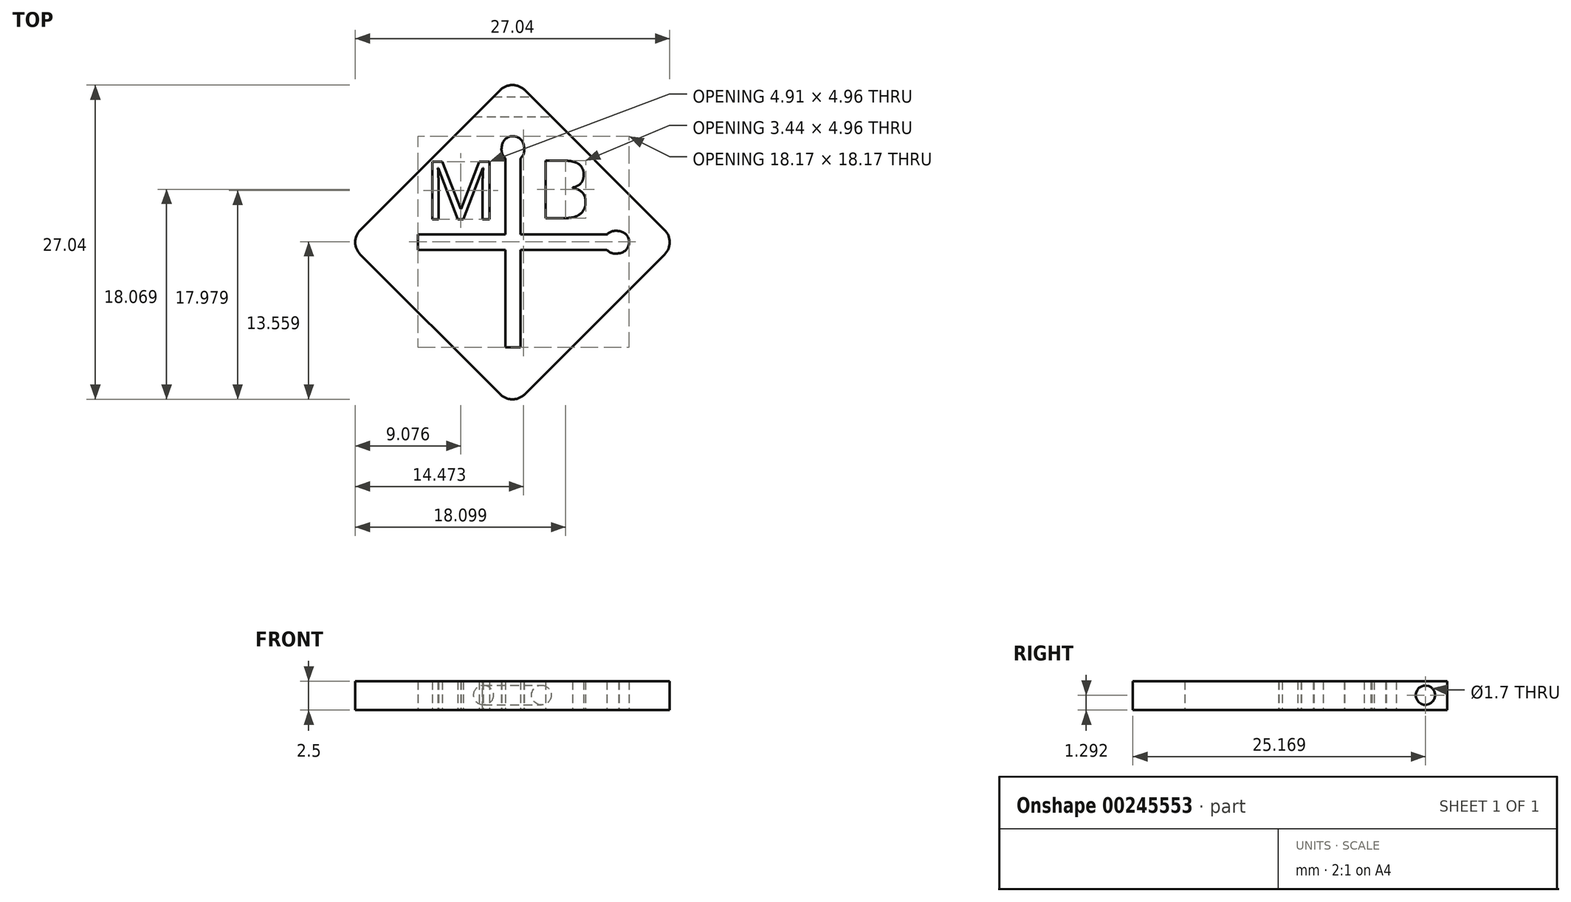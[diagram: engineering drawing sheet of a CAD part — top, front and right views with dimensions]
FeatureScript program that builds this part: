
annotation { "Feature Type Name" : "Feature", "Feature Type Description" : "" }
export const myFeature = defineFeature(function(context is Context, id is Id, definition is map)
    precondition{}
    {
        {
            var Q0;
            Q0=qCreatedBy(makeId("Top.planeOp"),FACE);
            var sketch = newSketch(context, id + "F0", { "sketchPlane" : qUnion([Q0])});
            skLineSegment(sketch, "E0", {"start": v(1.06, -1.06) * mm, "end": v(13.08, -13.08) * mm});
            skLineSegment(sketch, "E1", {"start": v(13.08, -15.2) * mm, "end": v(1.06, -27.22) * mm});
            skLineSegment(sketch, "E2", {"start": v(-1.06, -27.22) * mm, "end": v(-13.08, -15.2) * mm});
            skLineSegment(sketch, "E3", {"start": v(-13.08, -13.08) * mm, "end": v(-1.06, -1.06) * mm});
            skPoint(sketch, "E4.visualSharp", {"position": v(0, 0) * mm});
            skArc(sketch, "E4.filletArc", {"start": v(1.06, -1.06) * mm, "mid": v(0, -0.62) * mm, "end": v(-1.06, -1.06) * mm});
            skPoint(sketch, "E5.visualSharp", {"position": v(-14.14, -14.14) * mm});
            skArc(sketch, "E5.filletArc", {"start": v(-13.08, -13.08) * mm, "mid": v(-13.52, -14.14) * mm, "end": v(-13.08, -15.2) * mm});
            skPoint(sketch, "E6.visualSharp", {"position": v(14.14, -14.14) * mm});
            skArc(sketch, "E6.filletArc", {"start": v(13.08, -15.2) * mm, "mid": v(13.52, -14.14) * mm, "end": v(13.08, -13.08) * mm});
            skPoint(sketch, "E7.visualSharp", {"position": v(0, -28.28) * mm});
            skArc(sketch, "E7.filletArc", {"start": v(-1.06, -27.22) * mm, "mid": v(0, -27.66) * mm, "end": v(1.06, -27.22) * mm});
            skLineSegment(sketch, "E8", {"start": v(0, 0) * mm, "end": v(0, -31.86) * mm, "construction": true});
            skLineSegment(sketch, "E9", {"start": v(-14.14, -14.14) * mm, "end": v(14.14, -14.14) * mm, "construction": true});
            skLineSegment(sketch, "E10", {"start": v(-8.13, -13.48) * mm, "end": v(-8.13, -14.8) * mm});
            skLineSegment(sketch, "E11", {"start": v(-8.13, -14.8) * mm, "end": v(8.13, -14.8) * mm});
            skLineSegment(sketch, "E12", {"start": v(8.13, -13.48) * mm, "end": v(-8.13, -13.48) * mm});
            skLineSegment(sketch, "E13", {"start": v(-8.13, -13.48) * mm, "end": v(0, -13.48) * mm, "construction": true});
            skLineSegment(sketch, "E14", {"start": v(0, -13.48) * mm, "end": v(8.13, -13.48) * mm, "construction": true});
            skArc(sketch, "E15", {"start": v(9.18, -15.1) * mm, "mid": v(10.04, -14.12) * mm, "end": v(9.13, -13.2) * mm});
            skArc(sketch, "E16", {"start": v(9.13, -13.2) * mm, "mid": v(8.6, -13.2) * mm, "end": v(8.13, -13.48) * mm});
            skArc(sketch, "E17", {"start": v(8.13, -14.8) * mm, "mid": v(8.61, -15.1) * mm, "end": v(9.18, -15.1) * mm});
            skLineSegment(sketch, "E18", {"start": v(-0.62, -23.19) * mm, "end": v(0.7, -23.19) * mm});
            skLineSegment(sketch, "E19", {"start": v(0.7, -23.19) * mm, "end": v(0.7, -6.92) * mm});
            skLineSegment(sketch, "E20", {"start": v(-0.62, -6.92) * mm, "end": v(-0.62, -23.19) * mm});
            skLineSegment(sketch, "E21", {"start": v(-0.62, -23.19) * mm, "end": v(-0.62, -15.05) * mm, "construction": true});
            skLineSegment(sketch, "E22", {"start": v(-0.62, -15.05) * mm, "end": v(-0.62, -6.92) * mm, "construction": true});
            skArc(sketch, "E23", {"start": v(0.99, -5.88) * mm, "mid": v(0.02, -5.01) * mm, "end": v(-0.91, -5.92) * mm});
            skArc(sketch, "E24", {"start": v(-0.91, -5.92) * mm, "mid": v(-0.9, -6.46) * mm, "end": v(-0.62, -6.92) * mm});
            skArc(sketch, "E25", {"start": v(0.7, -6.92) * mm, "mid": v(1, -6.44) * mm, "end": v(0.99, -5.88) * mm});
            skText(sketch, "E26", { "text": "M", "fontName": "OpenSans-Regular.ttf"});
            skText(sketch, "E27", { "text": "B", "fontName": "OpenSans-Regular.ttf"});
            skPoint(sketch, "E28", {"position": v(7.07, -7.07) * mm});
            const initialGuessF0  = {"E26": [-0.00758, -0.01216, 1, 0, 0.005], "E27": [0.00218, -0.01207, 1, 0, 0.005]};
            skSetInitialGuess(sketch, initialGuessF0);
            skSolve(sketch);
        }
        {
            var Q0;
            Q0=makeQuery(id+"F0.imprint","IMPRINT",FACE,{"disambiguationData":[TD([[makeQuery(id+"F0.imprint","IMPRINT",EDGE,{"derivedFrom":sQuery(id+"F0.wireOp",EDGE,"E0")}),-1.0]])]});
            extrude(context, id + "F1", {"entities" : qUnion([Q0]), "depth" : 2.5 * mm});
        }
        {
            var Q0;
            Q0=qCreatedBy(makeId("Right.planeOp"),FACE);
            var sketch = newSketch(context, id + "F2", { "sketchPlane" : qUnion([Q0])});
            skCircle(sketch, "E29", {"center": v(-2.5, 1.3) * mm, "radius": 0.85 * mm});
            skSolve(sketch);
        }
        {
            var Q0;
            Q0=qSketchRegion(id+"F2",true);
            extrude(context, id + "F3", {"entities" : qUnion([Q0]), "operationType" : NewBodyOperationType.REMOVE, "endBound" : BoundingType.SYMMETRIC, "oppositeDirection" : true, "depth" : 25 * mm});
        }
    });
